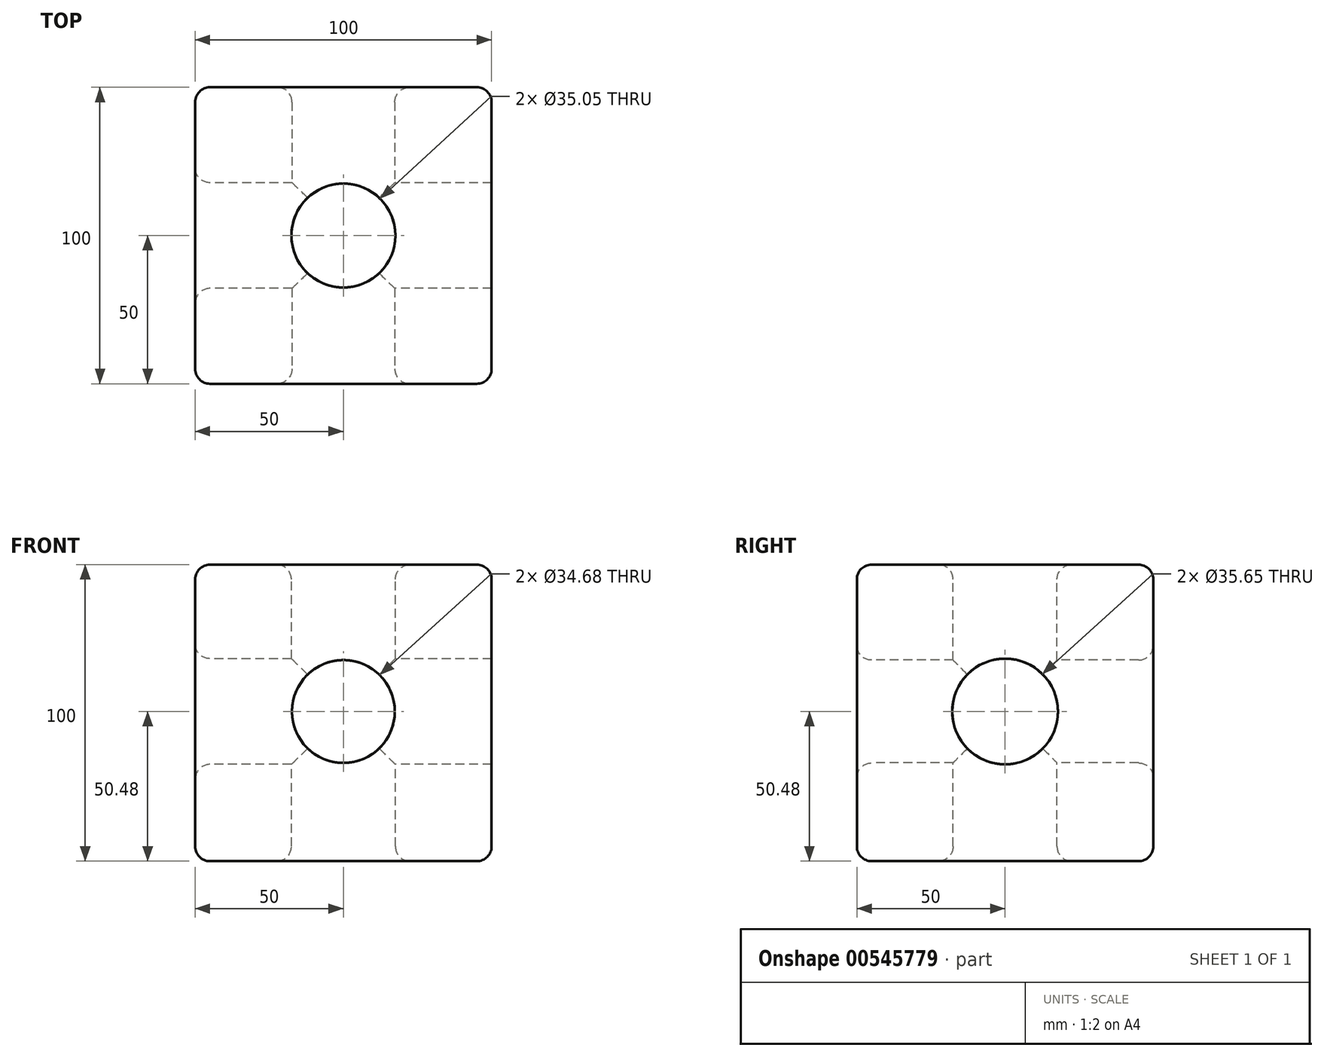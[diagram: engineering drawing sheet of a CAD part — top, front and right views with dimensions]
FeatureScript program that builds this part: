
annotation { "Feature Type Name" : "Feature", "Feature Type Description" : "" }
export const myFeature = defineFeature(function(context is Context, id is Id, definition is map)
    precondition{}
    {
        {
            var Q0;
            Q0=qCreatedBy(makeId("Front.planeOp"),FACE);
            var sketch = newSketch(context, id + "F0", { "sketchPlane" : qUnion([Q0])});
            skLineSegment(sketch, "E0.bottom", {"start": v(50, 49.52) * mm, "end": v(-50, 49.52) * mm});
            skLineSegment(sketch, "E0.top", {"start": v(50, -50.48) * mm, "end": v(-50, -50.48) * mm});
            skLineSegment(sketch, "E0.left", {"start": v(50, 49.52) * mm, "end": v(50, -50.48) * mm});
            skLineSegment(sketch, "E0.right", {"start": v(-50, 49.52) * mm, "end": v(-50, -50.48) * mm});
            skSolve(sketch);
        }
        {
            var Q0;
            Q0 = qSketchRegion(id + "F0", true);
            extrude(context, id + "F1", {"entities" : qUnion([Q0]), "endBound" : BoundingType.SYMMETRIC, "depth" : 100 * mm, "offsetDistance" : 25 * mm});
        }
        {
            var Q0;
            Q0=makeQuery(id+"F1.opExtrude","CAP_FACE",FACE,{"disambiguationData":[OSD([sQuery(id+"F0.wireOp",EDGE,"E0.bottom"),sQuery(id+"F0.wireOp",EDGE,"E0.top"),sQuery(id+"F0.wireOp",EDGE,"E0.left"),sQuery(id+"F0.wireOp",EDGE,"E0.right")])],"isStart":false});
            var sketch = newSketch(context, id + "F2", { "sketchPlane" : qUnion([Q0])});
            skCircle(sketch, "E1", {"center": v(0, 0) * mm, "radius": 17.34 * mm});
            skSolve(sketch);
        }
        {
            var Q0;
            Q0=makeQuery(id+"F2.imprint","IMPRINT",FACE,{"disambiguationData":[TD([[makeQuery(id+"F2.imprint","IMPRINT",EDGE,{"derivedFrom":sQuery(id+"F2.wireOp",EDGE,"E1")}),1.0]])]});
            extrude(context, id + "F3", {"entities" : qUnion([Q0]), "operationType" : NewBodyOperationType.REMOVE, "endBound" : BoundingType.UP_TO_NEXT, "oppositeDirection" : true, "depth" : 35 * mm, "offsetDistance" : 25 * mm});
        }
        {
            var Q0;
            Q0=makeQuery(id+"F1.opExtrude","SWEPT_FACE",FACE,{"disambiguationData":[OSD([sQuery(id+"F0.wireOp",EDGE,"E0.right")])]});
            var sketch = newSketch(context, id + "F4", { "sketchPlane" : qUnion([Q0])});
            skCircle(sketch, "E2", {"center": v(0, 0) * mm, "radius": 17.82 * mm});
            skSolve(sketch);
        }
        {
            var Q0;
            Q0=makeQuery(id+"F4.imprint","IMPRINT",FACE,{"disambiguationData":[TD([[makeQuery(id+"F4.imprint","IMPRINT",EDGE,{"derivedFrom":sQuery(id+"F4.wireOp",EDGE,"E2")}),1.0]])]});
            extrude(context, id + "F5", {"entities" : qUnion([Q0]), "operationType" : NewBodyOperationType.REMOVE, "oppositeDirection" : true, "depth" : 100 * mm, "offsetDistance" : 25 * mm});
        }
        {
            var Q0;
            Q0=makeQuery(id+"F1.opExtrude","SWEPT_FACE",FACE,{"disambiguationData":[OSD([sQuery(id+"F0.wireOp",EDGE,"E0.bottom")])]});
            var sketch = newSketch(context, id + "F6", { "sketchPlane" : qUnion([Q0])});
            skCircle(sketch, "E3", {"center": v(0, 0) * mm, "radius": 17.53 * mm});
            skSolve(sketch);
        }
        {
            var Q0;
            Q0=makeQuery(id+"F6.imprint","IMPRINT",FACE,{"disambiguationData":[TD([[makeQuery(id+"F6.imprint","IMPRINT",EDGE,{"derivedFrom":sQuery(id+"F6.wireOp",EDGE,"E3")}),1.0]])]});
            extrude(context, id + "F7", {"entities" : qUnion([Q0]), "operationType" : NewBodyOperationType.REMOVE, "oppositeDirection" : true, "depth" : 100 * mm, "offsetDistance" : 25 * mm});
        }
        {
            var Q0;
            Q0=makeQuery(id+"F1.opExtrude","CAP_EDGE",EDGE,{"disambiguationData":[OSD([sQuery(id+"F0.wireOp",EDGE,"E0.right")])],"isStart":true});
            var Q1;
            Q1=makeQuery(id+"F1.opExtrude","SWEPT_EDGE",EDGE,{"disambiguationData":[OSD([sQuery(id+"F0.wireOp",EDGE,"E0.top"),sQuery(id+"F0.wireOp",EDGE,"E0.right")])]});
            var Q2;
            Q2=makeQuery(id+"F1.opExtrude","CAP_EDGE",EDGE,{"disambiguationData":[OSD([sQuery(id+"F0.wireOp",EDGE,"E0.right")])],"isStart":false});
            var Q3;
            Q3=makeQuery(id+"F1.opExtrude","SWEPT_EDGE",EDGE,{"disambiguationData":[OSD([sQuery(id+"F0.wireOp",EDGE,"E0.bottom"),sQuery(id+"F0.wireOp",EDGE,"E0.right")])]});
            var Q4;
            Q4=makeQuery(id+"F1.opExtrude","CAP_EDGE",EDGE,{"disambiguationData":[OSD([sQuery(id+"F0.wireOp",EDGE,"E0.top")])],"isStart":true});
            var Q5;
            Q5=makeQuery(id+"F1.opExtrude","CAP_FACE",FACE,{"disambiguationData":[OSD([sQuery(id+"F0.wireOp",EDGE,"E0.bottom"),sQuery(id+"F0.wireOp",EDGE,"E0.top"),sQuery(id+"F0.wireOp",EDGE,"E0.left"),sQuery(id+"F0.wireOp",EDGE,"E0.right")])],"isStart":true});
            var Q6;
            Q6=makeQuery(id+"F1.opExtrude","SWEPT_FACE",FACE,{"disambiguationData":[OSD([sQuery(id+"F0.wireOp",EDGE,"E0.top")])]});
            var Q7;
            Q7=makeQuery(id+"F1.opExtrude","CAP_FACE",FACE,{"disambiguationData":[OSD([sQuery(id+"F0.wireOp",EDGE,"E0.bottom"),sQuery(id+"F0.wireOp",EDGE,"E0.top"),sQuery(id+"F0.wireOp",EDGE,"E0.left"),sQuery(id+"F0.wireOp",EDGE,"E0.right")])],"isStart":false});
            var Q8;
            Q8=makeQuery(id+"F1.opExtrude","SWEPT_FACE",FACE,{"disambiguationData":[OSD([sQuery(id+"F0.wireOp",EDGE,"E0.bottom")])]});
            var Q9;
            Q9=makeQuery(id+"F1.opExtrude","SWEPT_FACE",FACE,{"disambiguationData":[OSD([sQuery(id+"F0.wireOp",EDGE,"E0.right")])]});
            fillet(context, id + "F8", {"entities" : qUnion([Q0, Q1, Q2, Q3, Q4, Q5, Q6, Q7, Q8, Q9]), "radius" : 5 * mm, "tangentPropagation" : true, "allowEdgeOverflow" : false});
        }
    });
